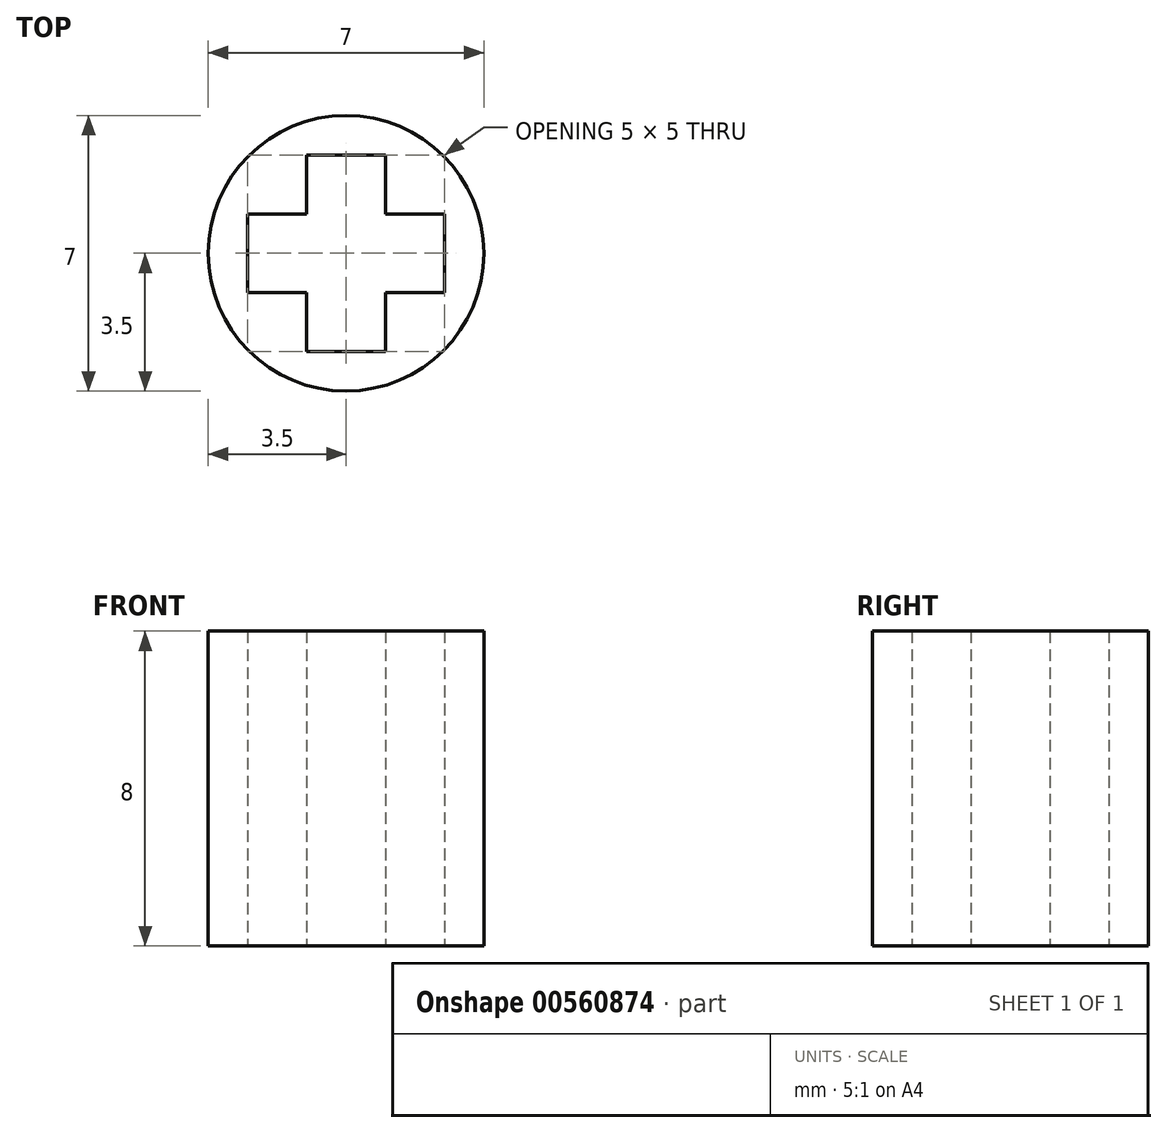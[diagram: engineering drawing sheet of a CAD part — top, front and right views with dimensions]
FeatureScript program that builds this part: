
annotation { "Feature Type Name" : "Feature", "Feature Type Description" : "" }
export const myFeature = defineFeature(function(context is Context, id is Id, definition is map)
    precondition{}
    {
        {
            var Q0;
            Q0=qCreatedBy(makeId("Top.planeOp"),FACE);
            var sketch = newSketch(context, id + "F0", { "sketchPlane" : qUnion([Q0])});
            skCircle(sketch, "E0", {"center": v(0, 0) * mm, "radius": 3.5 * mm});
            skLineSegment(sketch, "E1", {"start": v(0, 0) * mm, "end": v(0, -2.5) * mm});
            skLineSegment(sketch, "E2", {"start": v(0, -2.5) * mm, "end": v(-1, -2.5) * mm});
            skLineSegment(sketch, "E3", {"start": v(0, -2.5) * mm, "end": v(1, -2.5) * mm});
            skLineSegment(sketch, "E4", {"start": v(-1, -2.5) * mm, "end": v(-1, -1) * mm});
            skLineSegment(sketch, "E5", {"start": v(1, -2.5) * mm, "end": v(1, -1) * mm});
            skLineSegment(sketch, "E6", {"start": v(-1, -1) * mm, "end": v(-2.5, -1) * mm});
            skLineSegment(sketch, "E7", {"start": v(1, -1) * mm, "end": v(2.5, -1) * mm});
            skLineSegment(sketch, "E8", {"start": v(-2.5, -1) * mm, "end": v(-2.5, 1) * mm});
            skLineSegment(sketch, "E9", {"start": v(2.5, -1) * mm, "end": v(2.5, 1) * mm});
            skLineSegment(sketch, "E10", {"start": v(-2.5, 1) * mm, "end": v(-1, 1) * mm});
            skLineSegment(sketch, "E11", {"start": v(2.5, 1) * mm, "end": v(1, 1) * mm});
            skLineSegment(sketch, "E12", {"start": v(-1, 1) * mm, "end": v(-1, 2.5) * mm});
            skLineSegment(sketch, "E13", {"start": v(1, 1) * mm, "end": v(1, 2.5) * mm});
            skLineSegment(sketch, "E14", {"start": v(-1, 2.5) * mm, "end": v(1, 2.5) * mm});
            skSolve(sketch);
        }
        {
            var Q0;
            Q0 = qSketchRegion(id + "F0", true);
            extrude(context, id + "F1", {"entities" : qUnion([Q0]), "depth" : 8 * mm, "offsetDistance" : 25.4 * mm});
        }
    });
